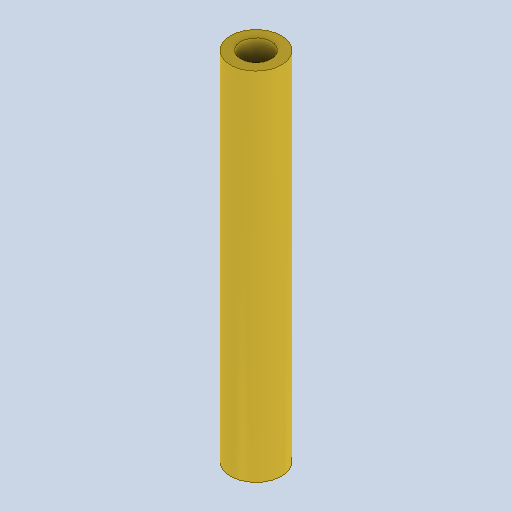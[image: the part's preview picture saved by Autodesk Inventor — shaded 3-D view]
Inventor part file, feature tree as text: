
AUTODESK INVENTOR PART (.ipt)
format: ipt  version: 2023 (Build 270158000, 158)  size: 80,896 bytes
history: native  units: in
note: dims shown in document units (in); Inventor stores cm internally (conversion verified against a paired STEP export)
features: other x3, sketch x1
ambient origin geometry x8: Origin, YZ Plane, XZ Plane, XY Plane, X Axis, Y Axis, Z Axis, Center Point
bodies: Solid1 (feature_tree)
feature tree (4):
  other  "Trudong35.ipt"
  other  "Solid1::Trudong35.ipt"
  other  "TaggingFeature1"
  sketch  "Sketch1"  dims[d0=0.3937in]
